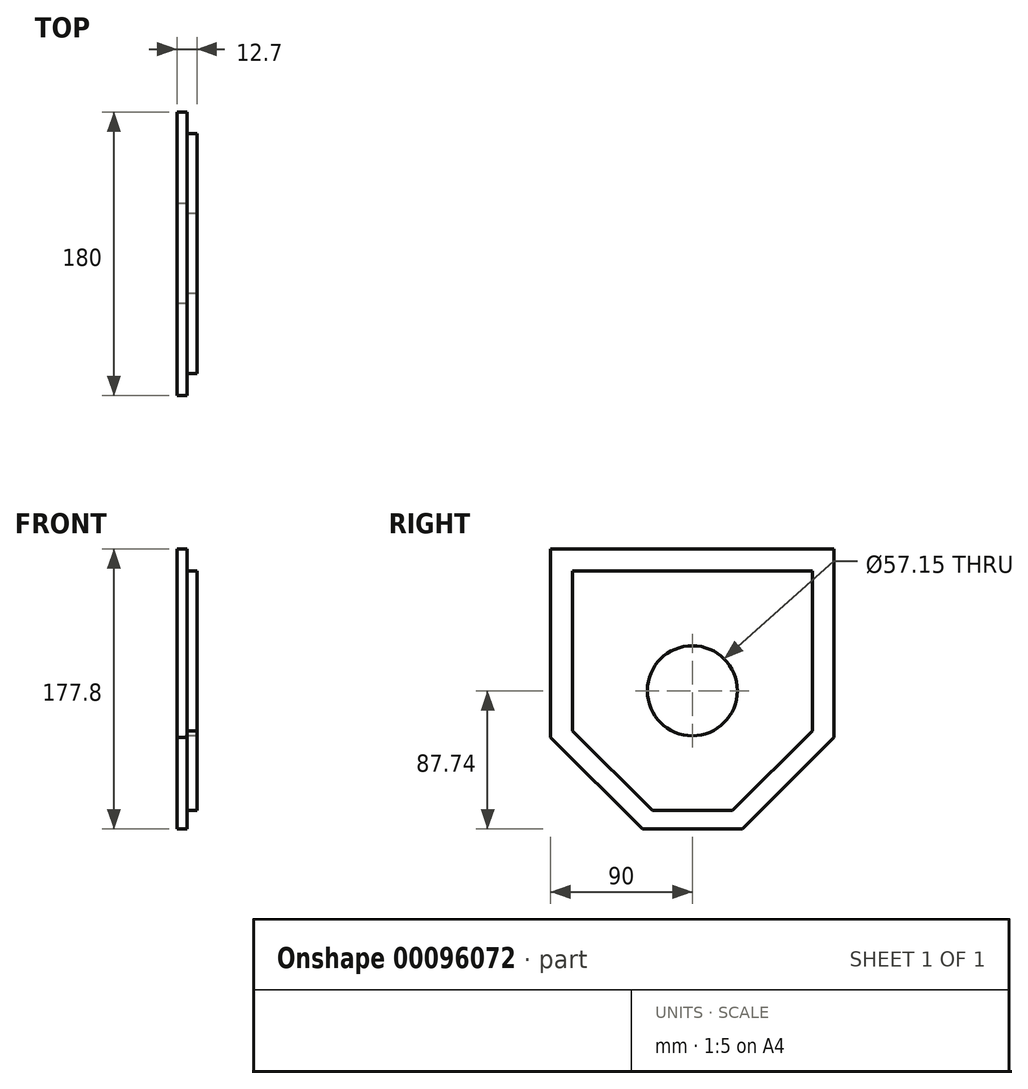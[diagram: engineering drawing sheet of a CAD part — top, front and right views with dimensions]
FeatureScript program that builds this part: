
annotation { "Feature Type Name" : "Feature", "Feature Type Description" : "" }
export const myFeature = defineFeature(function(context is Context, id is Id, definition is map)
    precondition{}
    {
        {
            var Q0;
            Q0=qCreatedBy(makeId("Right.planeOp"),FACE);
            var sketch = newSketch(context, id + "F0", { "sketchPlane" : qUnion([Q0])});
            skLineSegment(sketch, "E0.bottom", {"start": v(-25.4, -76.14) * mm, "end": v(25.4, -76.14) * mm});
            skLineSegment(sketch, "E0.top", {"start": v(-76.2, 76.14) * mm, "end": v(76.2, 76.14) * mm});
            skLineSegment(sketch, "E0.left", {"start": v(-76.2, -25.46) * mm, "end": v(-76.2, 76.14) * mm});
            skLineSegment(sketch, "E0.right", {"start": v(76.2, -25.46) * mm, "end": v(76.2, 76.14) * mm});
            skPoint(sketch, "E0.middle", {"position": v(0, 0) * mm});
            skLineSegment(sketch, "E1", {"start": v(76.2, -25.46) * mm, "end": v(25.4, -76.14) * mm});
            skLineSegment(sketch, "E2", {"start": v(-76.2, -25.46) * mm, "end": v(-25.4, -76.14) * mm});
            skPoint(sketch, "E3.orphan", {"position": v(76.2, -76.14) * mm});
            skPoint(sketch, "E4.orphan", {"position": v(-76.2, -76.14) * mm});
            skCircle(sketch, "E5", {"center": v(0, 0) * mm, "radius": 28.58 * mm});
            skLineSegment(sketch, "E6", {"start": v(77.3, 89.93) * mm, "end": v(-77.3, 90.06) * mm});
            skLineSegment(sketch, "E7", {"start": v(90, 77.23) * mm, "end": v(90, -29.64) * mm});
            skLineSegment(sketch, "E8", {"start": v(31.75, -87.74) * mm, "end": v(90, -29.64) * mm});
            skLineSegment(sketch, "E9", {"start": v(-31.75, -87.74) * mm, "end": v(31.75, -87.74) * mm});
            skLineSegment(sketch, "E10", {"start": v(-77.3, 90.06) * mm, "end": v(-90, 90.06) * mm});
            skLineSegment(sketch, "E11", {"start": v(-90, 90.06) * mm, "end": v(-90, -29.64) * mm});
            skLineSegment(sketch, "E12", {"start": v(-90, -29.64) * mm, "end": v(-31.75, -87.74) * mm});
            skLineSegment(sketch, "E13", {"start": v(77.3, 89.93) * mm, "end": v(90, 89.93) * mm});
            skLineSegment(sketch, "E14", {"start": v(90, 89.93) * mm, "end": v(90, 77.23) * mm});
            skPoint(sketch, "E15.endSnap0", {"position": v(0, -87.74) * mm});
            skSolve(sketch);
        }
        {
            var Q0;
            Q0=makeQuery(id+"F0.imprint","IMPRINT",FACE,{"disambiguationData":[TD([[makeQuery(id+"F0.imprint","IMPRINT",EDGE,{"derivedFrom":sQuery(id+"F0.wireOp",EDGE,"E0.bottom")}),1.0]])]});
            extrude(context, id + "F1", {"entities" : qUnion([Q0]), "depth" : 12.7 * mm});
        }
        {
            var Q0;
            Q0=makeQuery(id+"F0.imprint","IMPRINT",FACE,{"disambiguationData":[TD([[makeQuery(id+"F0.imprint","IMPRINT",EDGE,{"derivedFrom":sQuery(id+"F0.wireOp",EDGE,"E0.bottom")}),-1.0]])]});
            extrude(context, id + "F2", {"entities" : qUnion([Q0]), "operationType" : NewBodyOperationType.ADD, "depth" : 6.35 * mm});
        }
    });
